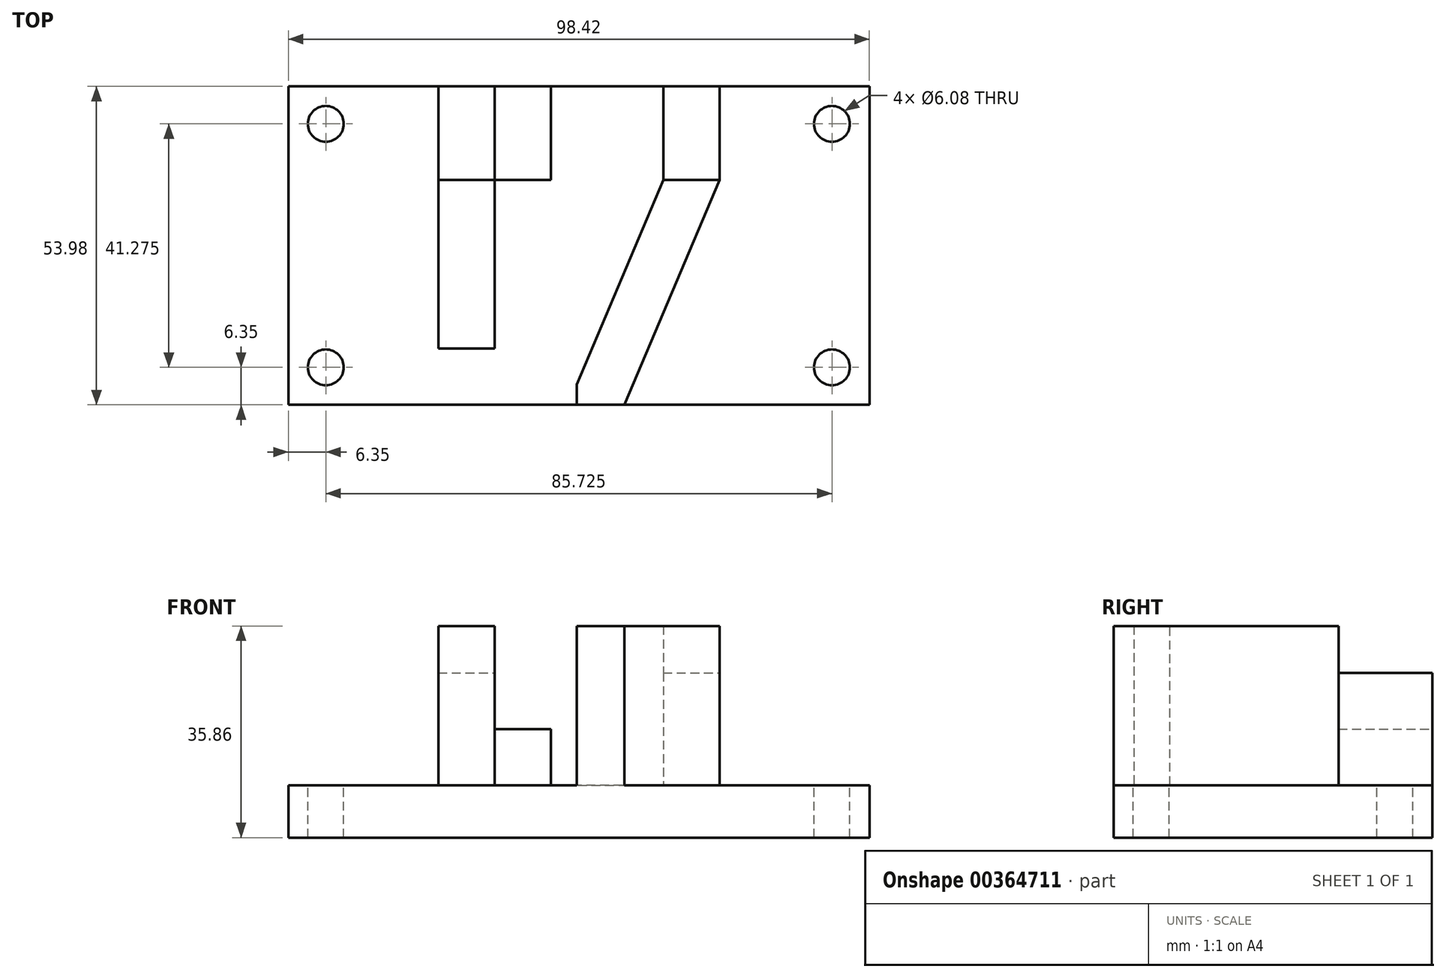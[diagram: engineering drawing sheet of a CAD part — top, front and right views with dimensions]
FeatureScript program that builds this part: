
annotation { "Feature Type Name" : "Feature", "Feature Type Description" : "" }
export const myFeature = defineFeature(function(context is Context, id is Id, definition is map)
    precondition{}
    {
        {
            var Q0;
            Q0=qCreatedBy(makeId("Top.planeOp"),FACE);
            var sketch = newSketch(context, id + "F0", { "sketchPlane" : qUnion([Q0])});
            skLineSegment(sketch, "E0.bottom", {"start": v(0, 0) * mm, "end": v(98.42, 0) * mm});
            skLineSegment(sketch, "E0.top", {"start": v(0, 53.97) * mm, "end": v(98.42, 53.97) * mm});
            skLineSegment(sketch, "E0.left", {"start": v(0, 0) * mm, "end": v(0, 53.97) * mm});
            skLineSegment(sketch, "E0.right", {"start": v(98.42, 0) * mm, "end": v(98.42, 53.97) * mm});
            skSolve(sketch);
        }
        {
            var Q0;
            Q0 = qSketchRegion(id + "F0", true);
            extrude(context, id + "F1", {"entities" : qUnion([Q0]), "depth" : 8.9 * mm});
        }
        {
            var Q0;
            Q0=makeQuery(id+"F1.opExtrude","CAP_FACE",FACE,{"disambiguationData":[OSD([sQuery(id+"F0.wireOp",EDGE,"E0.bottom"),sQuery(id+"F0.wireOp",EDGE,"E0.top"),sQuery(id+"F0.wireOp",EDGE,"E0.left"),sQuery(id+"F0.wireOp",EDGE,"E0.right")])],"isStart":false});
            var sketch = newSketch(context, id + "F2", { "sketchPlane" : qUnion([Q0])});
            skLineSegment(sketch, "E1", {"start": v(34.93, 0) * mm, "end": v(34.92, 38.1) * mm});
            skLineSegment(sketch, "E2", {"start": v(34.92, 38.1) * mm, "end": v(44.45, 38.1) * mm});
            skLineSegment(sketch, "E3", {"start": v(44.45, 38.1) * mm, "end": v(44.45, 53.97) * mm});
            skLineSegment(sketch, "E4", {"start": v(25.4, 0) * mm, "end": v(25.4, 53.97) * mm});
            skLineSegment(sketch, "E5", {"start": v(25.4, 53.97) * mm, "end": v(44.45, 53.97) * mm});
            skLineSegment(sketch, "E6", {"start": v(25.4, 0) * mm, "end": v(34.93, 0) * mm});
            skSolve(sketch);
        }
        {
            var Q0;
            Q0=makeQuery(id+"F2.imprint","IMPRINT",FACE,{"disambiguationData":[TD([[makeQuery(id+"F2.imprint","IMPRINT",EDGE,{"derivedFrom":sQuery(id+"F2.wireOp",EDGE,"E1")}),1.0]])]});
            extrude(context, id + "F3", {"entities" : qUnion([Q0]), "operationType" : NewBodyOperationType.ADD, "depth" : 9.52 * mm});
        }
        {
            var Q0;
            {var subQ0=sQuery(id+"F0.wireOp",EDGE,"E0.top");var subQ1=sQuery(id+"F0.wireOp",EDGE,"E0.right");var subQ2=sQuery(id+"F0.wireOp",EDGE,"E0.bottom");Q0=makeQuery(id+"F3.boolean.opBoolean","SPLIT",FACE,{"disambiguationData":[TD([makeQuery(id+"F1.opExtrude","SWEPT_FACE",FACE,{"disambiguationData":[OSD([subQ1])]})])],"derivedFrom":makeQuery(id+"F1.opExtrude","CAP_FACE",FACE,{"disambiguationData":[OSD([subQ2,subQ0,sQuery(id+"F0.wireOp",EDGE,"E0.left"),subQ1])],"isStart":false})});}
            var sketch = newSketch(context, id + "F4", { "sketchPlane" : qUnion([Q0])});
            skLineSegment(sketch, "E7", {"start": v(63.5, 53.97) * mm, "end": v(63.5, 38.1) * mm});
            skLineSegment(sketch, "E8", {"start": v(73.03, 38.1) * mm, "end": v(73.03, 53.97) * mm});
            skLineSegment(sketch, "E9", {"start": v(73.03, 53.97) * mm, "end": v(63.5, 53.98) * mm});
            skLineSegment(sketch, "E10", {"start": v(63.5, 38.1) * mm, "end": v(48.87, 3.42) * mm});
            skLineSegment(sketch, "E11", {"start": v(48.87, 3.42) * mm, "end": v(48.87, 0) * mm});
            skLineSegment(sketch, "E12", {"start": v(48.87, 0) * mm, "end": v(56.95, 0) * mm});
            skLineSegment(sketch, "E13", {"start": v(56.95, 0) * mm, "end": v(73.03, 38.1) * mm});
            skSolve(sketch);
        }
        {
            var Q0;
            Q0 = qSketchRegion(id + "F4", true);
            extrude(context, id + "F5", {"entities" : qUnion([Q0]), "operationType" : NewBodyOperationType.ADD, "depth" : 19.05 * mm});
        }
        {
            var Q0;
            Q0=makeQuery(id+"F5.opExtrude","CAP_FACE",FACE,{"disambiguationData":[OSD([sQuery(id+"F4.wireOp",EDGE,"E7"),sQuery(id+"F4.wireOp",EDGE,"E8"),sQuery(id+"F4.wireOp",EDGE,"E9"),sQuery(id+"F4.wireOp",EDGE,"E10"),sQuery(id+"F4.wireOp",EDGE,"E11"),sQuery(id+"F4.wireOp",EDGE,"E12"),sQuery(id+"F4.wireOp",EDGE,"E13")])],"isStart":false});
            var sketch = newSketch(context, id + "F6", { "sketchPlane" : qUnion([Q0])});
            skLineSegment(sketch, "E14.0", {"start": v(56.95, 0) * mm, "end": v(73.03, 38.1) * mm});
            skLineSegment(sketch, "E15.0", {"start": v(63.5, 38.1) * mm, "end": v(48.87, 3.42) * mm});
            skLineSegment(sketch, "E16", {"start": v(63.5, 38.1) * mm, "end": v(73.03, 38.1) * mm});
            skLineSegment(sketch, "E17.0", {"start": v(48.87, 0) * mm, "end": v(56.95, 0) * mm});
            skLineSegment(sketch, "E18.0", {"start": v(48.87, 3.42) * mm, "end": v(48.87, 0) * mm});
            skSolve(sketch);
        }
        {
            var Q0;
            Q0 = qSketchRegion(id + "F6", true);
            extrude(context, id + "F7", {"entities" : qUnion([Q0]), "operationType" : NewBodyOperationType.ADD, "depth" : 7.92 * mm});
        }
        {
            var Q0;
            Q0=makeQuery(id+"F3.opExtrude","CAP_FACE",FACE,{"disambiguationData":[OSD([sQuery(id+"F2.wireOp",EDGE,"E1"),sQuery(id+"F2.wireOp",EDGE,"E2"),sQuery(id+"F2.wireOp",EDGE,"E3"),sQuery(id+"F2.wireOp",EDGE,"E4"),sQuery(id+"F2.wireOp",EDGE,"E5"),sQuery(id+"F2.wireOp",EDGE,"E6")])],"isStart":false});
            var sketch = newSketch(context, id + "F8", { "sketchPlane" : qUnion([Q0])});
            skLineSegment(sketch, "E19.bottom", {"start": v(34.92, 0) * mm, "end": v(25.4, 0) * mm});
            skLineSegment(sketch, "E19.top", {"start": v(34.92, 53.97) * mm, "end": v(25.4, 53.97) * mm});
            skLineSegment(sketch, "E19.left", {"start": v(34.92, 0) * mm, "end": v(34.92, 53.97) * mm});
            skLineSegment(sketch, "E19.right", {"start": v(25.4, 0) * mm, "end": v(25.4, 53.97) * mm});
            skSolve(sketch);
        }
        {
            var Q0;
            Q0 = qSketchRegion(id + "F8", true);
            extrude(context, id + "F9", {"entities" : qUnion([Q0]), "operationType" : NewBodyOperationType.ADD, "depth" : 9.52 * mm});
        }
        {
            var Q0;
            Q0=makeQuery(id+"F9.opExtrude","CAP_FACE",FACE,{"disambiguationData":[OSD([sQuery(id+"F8.wireOp",EDGE,"E19.bottom"),sQuery(id+"F8.wireOp",EDGE,"E19.top"),sQuery(id+"F8.wireOp",EDGE,"E19.left"),sQuery(id+"F8.wireOp",EDGE,"E19.right")])],"isStart":false});
            var sketch = newSketch(context, id + "F10", { "sketchPlane" : qUnion([Q0])});
            skLineSegment(sketch, "E20.bottom", {"start": v(34.92, 0) * mm, "end": v(25.4, 0) * mm});
            skLineSegment(sketch, "E20.top", {"start": v(34.92, 38.1) * mm, "end": v(25.4, 38.1) * mm});
            skLineSegment(sketch, "E20.left", {"start": v(34.92, 0) * mm, "end": v(34.92, 38.1) * mm});
            skLineSegment(sketch, "E20.right", {"start": v(25.4, 0) * mm, "end": v(25.4, 38.1) * mm});
            skSolve(sketch);
        }
        {
            var Q0;
            Q0 = qSketchRegion(id + "F10", true);
            extrude(context, id + "F11", {"entities" : qUnion([Q0]), "operationType" : NewBodyOperationType.ADD, "depth" : 7.92 * mm});
        }
        {
            var Q0;
            {var subQ0=sQuery(id+"F0.wireOp",EDGE,"E0.left");var subQ1=sQuery(id+"F0.wireOp",EDGE,"E0.top");var subQ2=sQuery(id+"F0.wireOp",EDGE,"E0.bottom");Q0=makeQuery(id+"F3.boolean.opBoolean","SPLIT",FACE,{"disambiguationData":[TD([makeQuery(id+"F1.opExtrude","SWEPT_FACE",FACE,{"disambiguationData":[OSD([subQ0])]})])],"derivedFrom":makeQuery(id+"F1.opExtrude","CAP_FACE",FACE,{"disambiguationData":[OSD([subQ2,subQ1,subQ0,sQuery(id+"F0.wireOp",EDGE,"E0.right")])],"isStart":false})});}
            var sketch = newSketch(context, id + "F12", { "sketchPlane" : qUnion([Q0])});
            skCircle(sketch, "E21", {"center": v(6.35, 47.62) * mm, "radius": 3.04 * mm});
            skCircle(sketch, "E22", {"center": v(6.35, 6.35) * mm, "radius": 3.04 * mm});
            skCircle(sketch, "E23", {"center": v(92.08, 6.35) * mm, "radius": 3.04 * mm});
            skCircle(sketch, "E24", {"center": v(92.08, 47.62) * mm, "radius": 3.04 * mm});
            skSolve(sketch);
        }
        {
            var Q0;
            Q0 = qSketchRegion(id + "F12", true);
            extrude(context, id + "F13", {"entities" : qUnion([Q0]), "operationType" : NewBodyOperationType.REMOVE, "oppositeDirection" : true, "depth" : 25.4 * mm});
        }
        {
            var Q0;
            Q0=makeQuery(id+"F11.opExtrude","CAP_FACE",FACE,{"disambiguationData":[OSD([sQuery(id+"F10.wireOp",EDGE,"E20.bottom"),sQuery(id+"F10.wireOp",EDGE,"E20.top"),sQuery(id+"F10.wireOp",EDGE,"E20.left"),sQuery(id+"F10.wireOp",EDGE,"E20.right")])],"isStart":false});
            var sketch = newSketch(context, id + "F14", { "sketchPlane" : qUnion([Q0])});
            skLineSegment(sketch, "E25.bottom", {"start": v(25.4, 0) * mm, "end": v(34.93, 0) * mm});
            skLineSegment(sketch, "E25.top", {"start": v(25.4, 9.53) * mm, "end": v(34.93, 9.53) * mm});
            skLineSegment(sketch, "E25.left", {"start": v(25.4, 0) * mm, "end": v(25.4, 9.53) * mm});
            skLineSegment(sketch, "E25.right", {"start": v(34.93, 0) * mm, "end": v(34.93, 9.53) * mm});
            skSolve(sketch);
        }
        {
            var Q0;
            Q0 = qSketchRegion(id + "F14", true);
            var Q1;
            {var subQ0=sQuery(id+"F0.wireOp",EDGE,"E0.left");var subQ1=sQuery(id+"F0.wireOp",EDGE,"E0.top");var subQ2=sQuery(id+"F0.wireOp",EDGE,"E0.bottom");Q1=makeQuery(id+"F3.boolean.opBoolean","SPLIT",FACE,{"disambiguationData":[TD([makeQuery(id+"F1.opExtrude","SWEPT_FACE",FACE,{"disambiguationData":[OSD([subQ0])]})])],"derivedFrom":makeQuery(id+"F1.opExtrude","CAP_FACE",FACE,{"disambiguationData":[OSD([subQ2,subQ1,subQ0,sQuery(id+"F0.wireOp",EDGE,"E0.right")])],"isStart":false})});}
            extrude(context, id + "F15", {"entities" : qUnion([Q0]), "operationType" : NewBodyOperationType.REMOVE, "endBound" : BoundingType.UP_TO_SURFACE, "oppositeDirection" : true, "endBoundEntityFace" : qUnion([Q1]), "depth" : 25.4 * mm});
        }
    });
